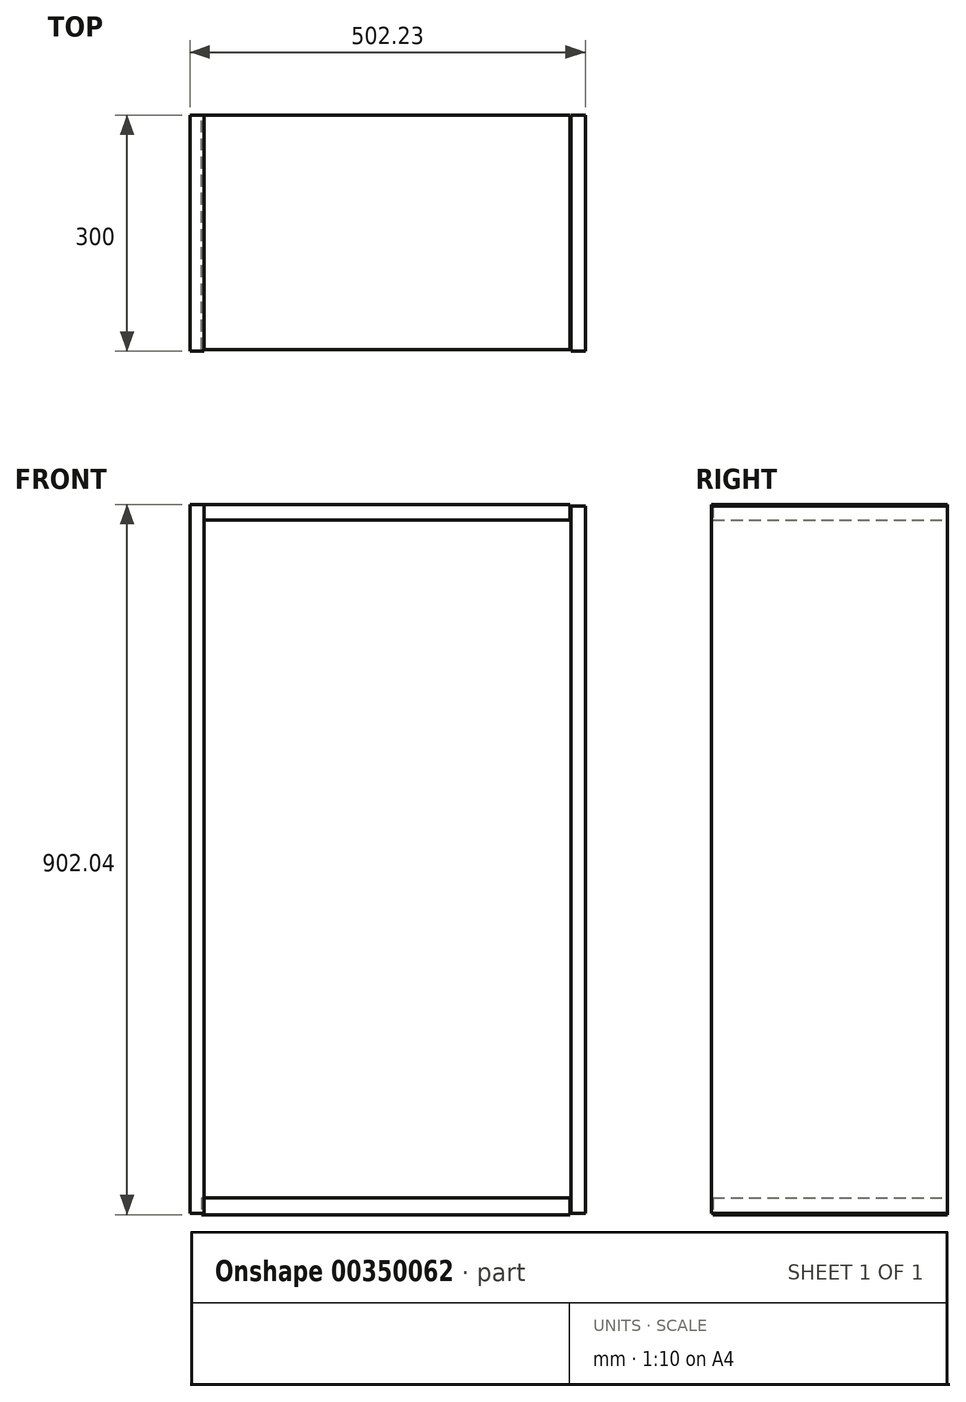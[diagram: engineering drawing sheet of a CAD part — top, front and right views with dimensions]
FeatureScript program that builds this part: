
annotation { "Feature Type Name" : "Feature", "Feature Type Description" : "" }
export const myFeature = defineFeature(function(context is Context, id is Id, definition is map)
    precondition{}
    {
        {
            var Q0;
            Q0=qCreatedBy(makeId("Front.planeOp"),FACE);
            var sketch = newSketch(context, id + "F0", { "sketchPlane" : qUnion([Q0])});
            skLineSegment(sketch, "E0.bottom", {"start": v(-251.94, 451.02) * mm, "end": v(-233.77, 451.02) * mm});
            skLineSegment(sketch, "E0.top", {"start": v(-251.94, -449.37) * mm, "end": v(-233.77, -449.37) * mm});
            skLineSegment(sketch, "E0.left", {"start": v(-251.94, 451.02) * mm, "end": v(-251.94, -449.37) * mm});
            skLineSegment(sketch, "E0.right", {"start": v(-233.77, 451.02) * mm, "end": v(-233.77, -449.37) * mm});
            skLineSegment(sketch, "E1.bottom", {"start": v(232.12, 449.37) * mm, "end": v(250.3, 449.37) * mm});
            skLineSegment(sketch, "E1.top", {"start": v(232.12, -449.37) * mm, "end": v(250.3, -449.37) * mm});
            skLineSegment(sketch, "E1.left", {"start": v(232.12, 449.37) * mm, "end": v(232.12, -449.37) * mm});
            skLineSegment(sketch, "E1.right", {"start": v(250.3, 449.37) * mm, "end": v(250.3, -449.37) * mm});
            skSolve(sketch);
        }
        {
            var Q0;
            Q0 = qSketchRegion(id + "F0", true);
            extrude(context, id + "F1", {"entities" : qUnion([Q0]), "depth" : 300 * mm});
        }
        {
            var Q0;
            Q0=qCreatedBy(makeId("Front.planeOp"),FACE);
            var sketch = newSketch(context, id + "F2", { "sketchPlane" : qUnion([Q0])});
            skLineSegment(sketch, "E2.bottom", {"start": v(-233.77, 451.02) * mm, "end": v(230.47, 451.02) * mm});
            skLineSegment(sketch, "E2.top", {"start": v(-233.77, 431.2) * mm, "end": v(230.47, 431.2) * mm});
            skLineSegment(sketch, "E2.left", {"start": v(-233.77, 451.02) * mm, "end": v(-233.77, 431.2) * mm});
            skLineSegment(sketch, "E2.right", {"start": v(230.47, 451.02) * mm, "end": v(230.47, 431.2) * mm});
            skLineSegment(sketch, "E3.bottom", {"start": v(-237.08, -429.55) * mm, "end": v(230.47, -429.55) * mm});
            skLineSegment(sketch, "E3.top", {"start": v(-237.08, -451.02) * mm, "end": v(230.47, -451.02) * mm});
            skLineSegment(sketch, "E3.left", {"start": v(-237.08, -429.55) * mm, "end": v(-237.08, -451.02) * mm});
            skLineSegment(sketch, "E3.right", {"start": v(230.47, -429.55) * mm, "end": v(230.47, -451.02) * mm});
            skSolve(sketch);
        }
        {
            var Q0;
            Q0 = qSketchRegion(id + "F2", true);
            extrude(context, id + "F3", {"entities" : qUnion([Q0]), "depth" : 298 * mm});
        }
    });
